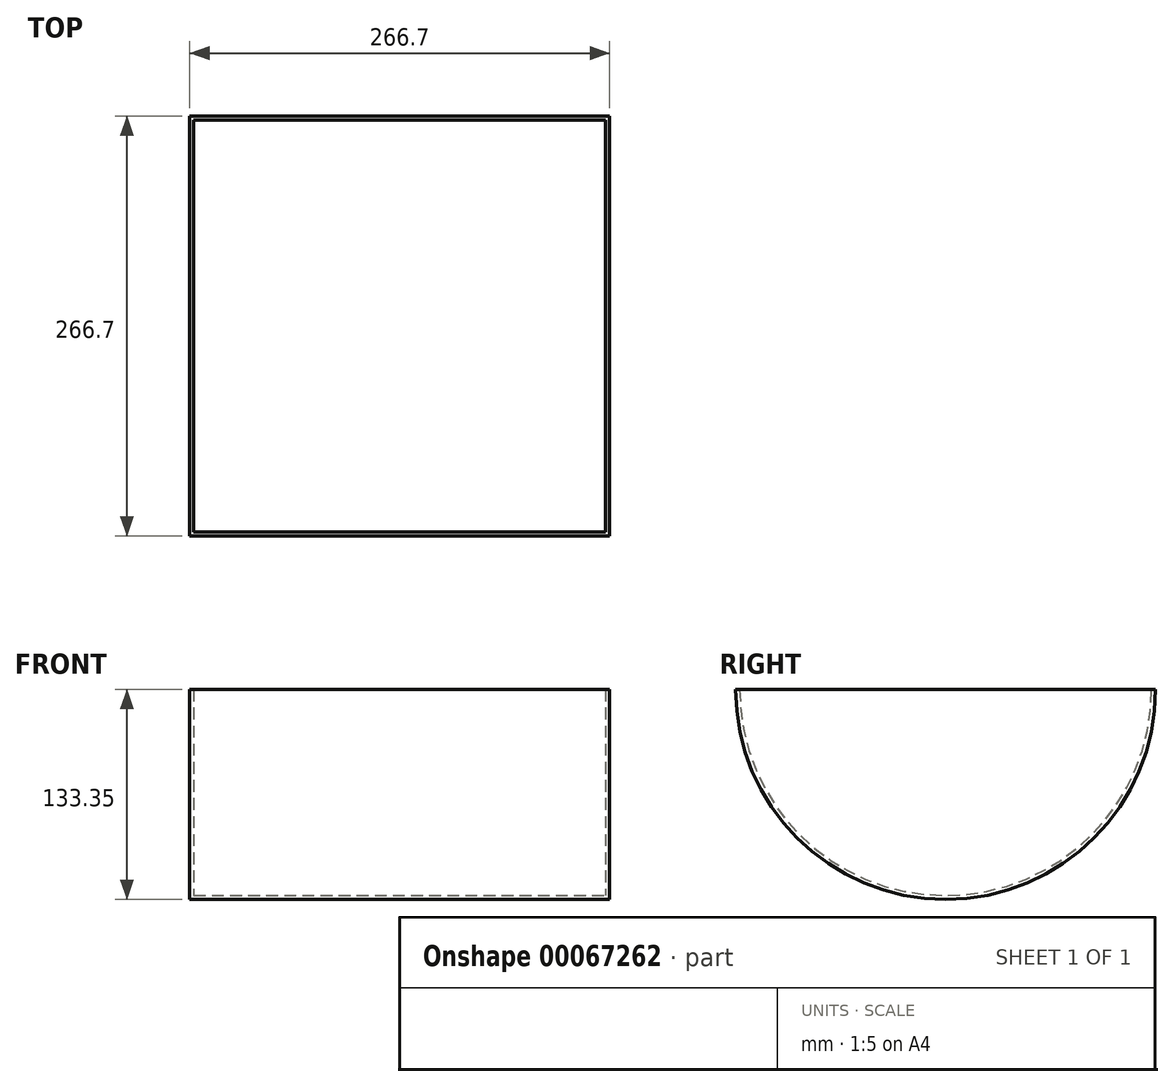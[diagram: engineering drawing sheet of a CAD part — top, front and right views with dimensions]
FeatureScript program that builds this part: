
annotation { "Feature Type Name" : "Feature", "Feature Type Description" : "" }
export const myFeature = defineFeature(function(context is Context, id is Id, definition is map)
    precondition{}
    {
        {
            var Q0;
            Q0=qCreatedBy(makeId("Right.planeOp"),FACE);
            var sketch = newSketch(context, id + "F0", { "sketchPlane" : qUnion([Q0])});
            skArc(sketch, "E0", {"start": v(-133.35, 0) * mm, "mid": v(0, -133.35) * mm, "end": v(133.35, 0) * mm});
            skLineSegment(sketch, "E1", {"start": v(-133.35, 0) * mm, "end": v(133.35, 0) * mm});
            skSolve(sketch);
        }
        {
            var Q0;
            Q0=makeQuery(id+"F0.imprint","IMPRINT",FACE,{"disambiguationData":[TD([[makeQuery(id+"F0.imprint","IMPRINT",EDGE,{"derivedFrom":sQuery(id+"F0.wireOp",EDGE,"E0")}),1.0]])]});
            extrude(context, id + "F1", {"entities" : qUnion([Q0]), "oppositeDirection" : true, "depth" : 266.7 * mm});
        }
        {
            var Q0;
            Q0=makeQuery(id+"F1.opExtrude","SWEPT_FACE",FACE,{"disambiguationData":[OSD([sQuery(id+"F0.wireOp",EDGE,"E1")])]});
            shell(context, id + "F2", {"entities" : qUnion([Q0]), "thickness" : 2.54 * mm});
        }
    });
